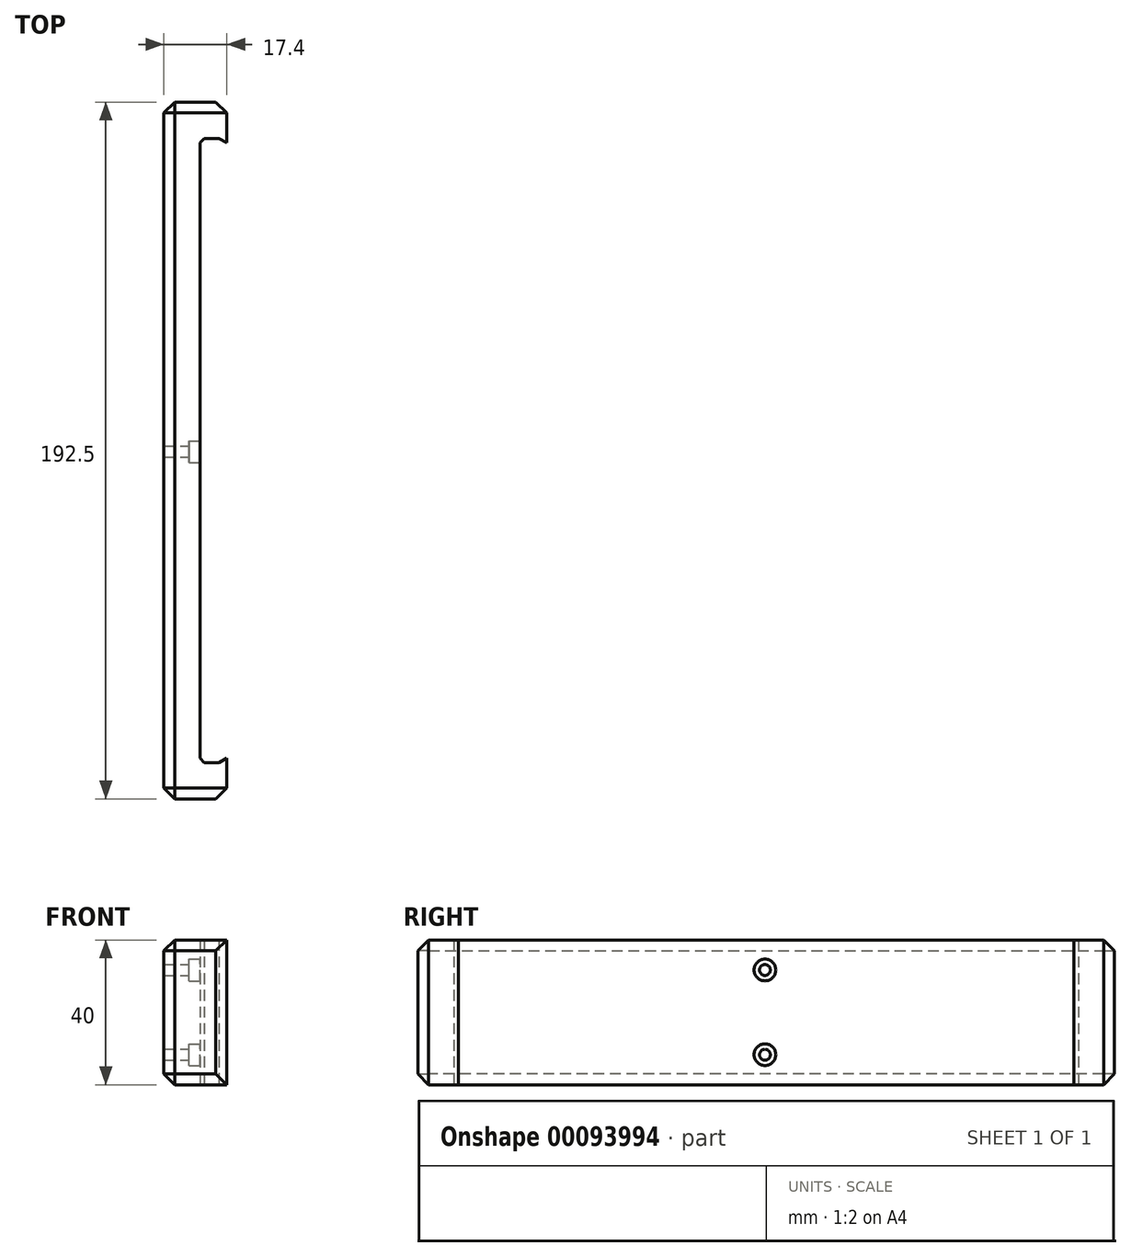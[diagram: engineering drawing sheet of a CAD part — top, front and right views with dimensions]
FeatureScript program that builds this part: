
annotation { "Feature Type Name" : "Feature", "Feature Type Description" : "" }
export const myFeature = defineFeature(function(context is Context, id is Id, definition is map)
    precondition{}
    {
        {
            var Q0;
            Q0=qCreatedBy(makeId("Top.planeOp"),FACE);
            var sketch = newSketch(context, id + "F0", { "sketchPlane" : qUnion([Q0])});
            skLineSegment(sketch, "E0.bottom", {"start": v(0, 86.57) * mm, "end": v(-10, 86.57) * mm});
            skLineSegment(sketch, "E0.top", {"start": v(0, -85.93) * mm, "end": v(-10, -85.93) * mm});
            skLineSegment(sketch, "E0.left", {"start": v(0, 86.57) * mm, "end": v(0, -85.93) * mm});
            skLineSegment(sketch, "E0.right", {"start": v(-10, 86.57) * mm, "end": v(-10, -85.93) * mm});
            skLineSegment(sketch, "E1.bottom", {"start": v(-10, 86.57) * mm, "end": v(7.4, 86.57) * mm});
            skLineSegment(sketch, "E1.top", {"start": v(-10, 96.57) * mm, "end": v(7.4, 96.57) * mm});
            skLineSegment(sketch, "E1.left", {"start": v(-10, 86.57) * mm, "end": v(-10, 96.57) * mm});
            skLineSegment(sketch, "E1.right", {"start": v(7.4, 86.57) * mm, "end": v(7.4, 96.57) * mm});
            skLineSegment(sketch, "E2.bottom", {"start": v(-10, -85.93) * mm, "end": v(7.4, -85.93) * mm});
            skLineSegment(sketch, "E2.top", {"start": v(-10, -95.93) * mm, "end": v(7.4, -95.93) * mm});
            skLineSegment(sketch, "E2.left", {"start": v(-10, -85.93) * mm, "end": v(-10, -95.93) * mm});
            skLineSegment(sketch, "E2.right", {"start": v(7.4, -85.93) * mm, "end": v(7.4, -95.93) * mm});
            skLineSegment(sketch, "E3", {"start": v(0, 86.57) * mm, "end": v(1.2, 86.57) * mm});
            skLineSegment(sketch, "E4", {"start": v(0, 86.57) * mm, "end": v(0, 85.37) * mm});
            skLineSegment(sketch, "E5", {"start": v(0, 85.37) * mm, "end": v(1.2, 86.57) * mm});
            skLineSegment(sketch, "E6", {"start": v(7.4, 86.57) * mm, "end": v(5.2, 86.57) * mm});
            skLineSegment(sketch, "E7", {"start": v(7.4, 86.57) * mm, "end": v(7.4, 85.37) * mm});
            skLineSegment(sketch, "E8", {"start": v(7.4, 85.37) * mm, "end": v(5.2, 86.57) * mm});
            skLineSegment(sketch, "E9", {"start": v(0, -85.93) * mm, "end": v(0, -84.73) * mm});
            skLineSegment(sketch, "E10", {"start": v(0, -85.93) * mm, "end": v(1.2, -85.93) * mm});
            skLineSegment(sketch, "E11", {"start": v(1.2, -85.93) * mm, "end": v(0, -84.73) * mm});
            skLineSegment(sketch, "E12", {"start": v(7.4, -85.93) * mm, "end": v(5.2, -85.93) * mm});
            skLineSegment(sketch, "E13", {"start": v(7.4, -85.93) * mm, "end": v(7.4, -84.73) * mm});
            skLineSegment(sketch, "E14", {"start": v(7.4, -84.73) * mm, "end": v(5.2, -85.93) * mm});
            skSolve(sketch);
        }
        {
            var Q0;
            Q0 = qSketchRegion(id + "F0", true);
            extrude(context, id + "F1", {"entities" : qUnion([Q0]), "depth" : 40 * mm});
        }
        {
            var Q0;
            Q0=makeQuery(id+"F1.opExtrude","SWEPT_BODY",BODY,{"disambiguationData":[OSD([sQuery(id+"F0.wireOp",EDGE,"E0.left"),sQuery(id+"F0.wireOp",EDGE,"E0.right"),sQuery(id+"F0.wireOp",EDGE,"E1.bottom"),sQuery(id+"F0.wireOp",EDGE,"E1.top"),sQuery(id+"F0.wireOp",EDGE,"E1.left"),sQuery(id+"F0.wireOp",EDGE,"E1.right"),sQuery(id+"F0.wireOp",EDGE,"E2.bottom"),sQuery(id+"F0.wireOp",EDGE,"E2.top"),sQuery(id+"F0.wireOp",EDGE,"E2.left"),sQuery(id+"F0.wireOp",EDGE,"E2.right"),sQuery(id+"F0.wireOp",EDGE,"E5"),sQuery(id+"F0.wireOp",EDGE,"E7"),sQuery(id+"F0.wireOp",EDGE,"E8"),sQuery(id+"F0.wireOp",EDGE,"E11"),sQuery(id+"F0.wireOp",EDGE,"E13"),sQuery(id+"F0.wireOp",EDGE,"E14")])]});
            transform(context, id + "F2", {"entities" : qUnion([Q0]), "transformType" : TransformType.TRANSLATION_3D, "dx" : 0 * mm, "dy" : 0 * mm, "dz" : -20 * mm, "makeCopy" : false});
        }
        {
            var Q0;
            Q0=makeQuery(id+"F1.opExtrude","SWEPT_FACE",FACE,{"disambiguationData":[OSD([sQuery(id+"F0.wireOp",EDGE,"E0.left")])]});
            var sketch = newSketch(context, id + "F3", { "sketchPlane" : qUnion([Q0])});
            skCircle(sketch, "E15", {"center": v(0, 11.7) * mm, "radius": 3 * mm});
            skCircle(sketch, "E16", {"center": v(0, -11.7) * mm, "radius": 3 * mm});
            skSolve(sketch);
        }
        {
            var Q0;
            Q0 = qSketchRegion(id + "F3", true);
            extrude(context, id + "F4", {"entities" : qUnion([Q0]), "operationType" : NewBodyOperationType.REMOVE, "oppositeDirection" : true, "depth" : 3 * mm});
        }
        {
            var Q0;
            Q0=makeQuery(id+"F1.opExtrude","SWEPT_FACE",FACE,{"disambiguationData":[OSD([sQuery(id+"F0.wireOp",EDGE,"E0.left")])]});
            var sketch = newSketch(context, id + "F5", { "sketchPlane" : qUnion([Q0])});
            skCircle(sketch, "E17", {"center": v(0, 11.7) * mm, "radius": 1.5 * mm});
            skCircle(sketch, "E18", {"center": v(0, -11.7) * mm, "radius": 1.5 * mm});
            skSolve(sketch);
        }
        {
            var Q0;
            Q0 = qSketchRegion(id + "F5", true);
            extrude(context, id + "F6", {"entities" : qUnion([Q0]), "operationType" : NewBodyOperationType.REMOVE, "oppositeDirection" : true, "depth" : 12 * mm});
        }
        {
            var Q0;
            Q0=makeQuery(id+"F1.opExtrude","CAP_EDGE",EDGE,{"disambiguationData":[OSD([sQuery(id+"F0.wireOp",EDGE,"E2.top")])],"isStart":false});
            var Q1;
            Q1=makeQuery(id+"F1.opExtrude","SWEPT_FACE",FACE,{"disambiguationData":[OSD([sQuery(id+"F0.wireOp",EDGE,"E2.top")])]});
            var Q2;
            Q2=makeQuery(id+"F1.opExtrude","SWEPT_FACE",FACE,{"disambiguationData":[OSD([sQuery(id+"F0.wireOp",EDGE,"E1.top")])]});
            var Q3;
            Q3=makeQuery(id+"F1.opExtrude","CAP_EDGE",EDGE,{"disambiguationData":[OSD([sQuery(id+"F0.wireOp",EDGE,"E0.right"),sQuery(id+"F0.wireOp",EDGE,"E1.left"),sQuery(id+"F0.wireOp",EDGE,"E2.left")])],"isStart":false});
            var Q4;
            Q4=makeQuery(id+"F1.opExtrude","CAP_EDGE",EDGE,{"disambiguationData":[OSD([sQuery(id+"F0.wireOp",EDGE,"E0.right"),sQuery(id+"F0.wireOp",EDGE,"E1.left"),sQuery(id+"F0.wireOp",EDGE,"E2.left")])],"isStart":true});
            chamfer(context, id + "F7", {"entities" : qUnion([Q0, Q1, Q2, Q3, Q4]), "width" : 3 * mm, "tangentPropagation" : true});
        }
    });
